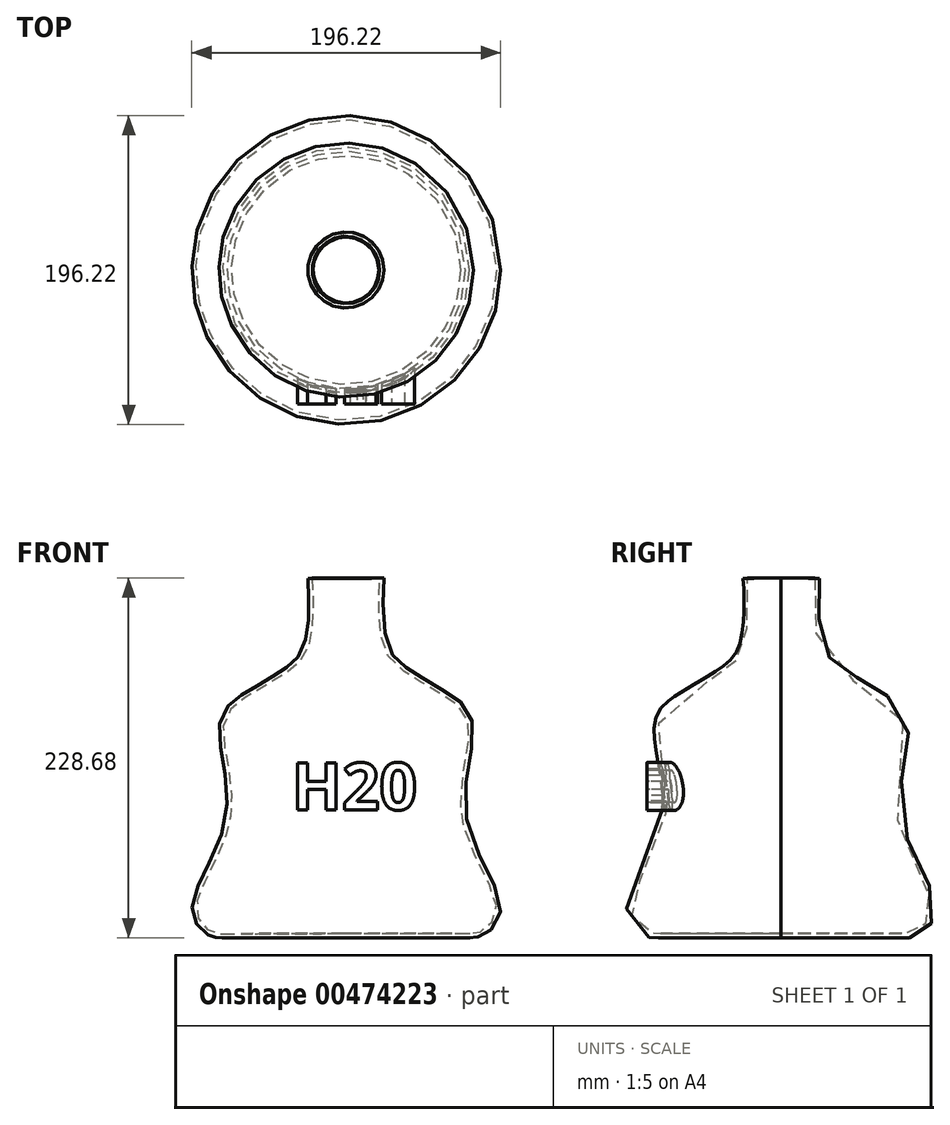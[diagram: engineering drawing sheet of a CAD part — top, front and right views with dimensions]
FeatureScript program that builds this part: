
annotation { "Feature Type Name" : "Feature", "Feature Type Description" : "" }
export const myFeature = defineFeature(function(context is Context, id is Id, definition is map)
    precondition{}
    {
        {
            var Q0;
            Q0=qCreatedBy(makeId("Front.planeOp"),FACE);
            var sketch = newSketch(context, id + "F0", { "sketchPlane" : qUnion([Q0])});
            skFitSpline(sketch, "E0", {"points": [v(0, 0) * mm, v(34.67, 0) * mm, v(59.42, 0) * mm, v(74.62, 0) * mm, v(80.36, 0) * mm, v(86.7, 1.46) * mm, v(98.07, 17.5) * mm, v(76.17, 76.9) * mm, v(79.96, 137.93) * mm, v(60.63, 157.65) * mm, v(39.03, 170.91) * mm, v(26.14, 186.45) * mm, v(23.9, 228.33) * mm], "startDerivative": vector(335.3, 0.36) * mm, "endDerivative": vector(16.6, 266.23) * mm});
            skFitSpline(sketch, "E1.0", {"points": [v(0, 2.7) * mm, v(3.5, 2.7) * mm, v(10.93, 2.7) * mm, v(20.66, 2.7) * mm, v(28.3, 2.7) * mm, v(33.86, 2.7) * mm, v(39.12, 2.7) * mm, v(44.12, 2.7) * mm, v(48.88, 2.7) * mm, v(53.45, 2.7) * mm, v(57.13, 2.7) * mm, v(60, 2.7) * mm, v(62.85, 2.7) * mm, v(66.27, 2.7) * mm, v(69.44, 2.71) * mm, v(71.75, 2.7) * mm, v(73.36, 2.7) * mm, v(74.82, 2.7) * mm, v(76.13, 2.69) * mm, v(77.3, 2.68) * mm, v(78.39, 2.67) * mm, v(79.23, 2.68) * mm, v(79.9, 2.69) * mm, v(80.4, 2.7) * mm, v(80.88, 2.71) * mm, v(81.5, 2.75) * mm, v(82.24, 2.82) * mm, v(83.13, 2.98) * mm, v(84.1, 3.26) * mm, v(85, 3.63) * mm, v(85.81, 4.03) * mm, v(86.68, 4.52) * mm, v(87.85, 5.28) * mm, v(89.28, 6.4) * mm, v(90.69, 7.7) * mm, v(92, 9.19) * mm, v(93.18, 10.83) * mm, v(94.16, 12.6) * mm, v(94.88, 14.5) * mm, v(95.33, 16.53) * mm, v(95.44, 18.67) * mm, v(95.2, 21.08) * mm, v(94.64, 23.73) * mm, v(93.76, 26.58) * mm, v(92.6, 29.63) * mm, v(90.75, 33.9) * mm, v(87.96, 39.63) * mm, v(84.22, 47) * mm, v(80.47, 54.78) * mm, v(77.62, 61.57) * mm, v(75.7, 67.16) * mm, v(74.5, 71.43) * mm, v(73.73, 75.04) * mm, v(73.28, 77.96) * mm, v(72.93, 80.88) * mm, v(72.7, 84.52) * mm, v(72.68, 90.32) * mm, v(73.21, 97.46) * mm, v(74.39, 105.77) * mm, v(75.78, 113.68) * mm, v(77.05, 121.08) * mm, v(77.76, 126.7) * mm, v(77.97, 130.76) * mm, v(77.92, 133.58) * mm, v(77.68, 135.7) * mm, v(77.36, 137.27) * mm, v(76.96, 138.75) * mm, v(76.29, 140.48) * mm, v(75.24, 142.4) * mm, v(73.97, 144.21) * mm, v(71.98, 146.48) * mm, v(69.01, 149.1) * mm, v(65.57, 151.48) * mm, v(62.65, 153.3) * mm, v(60.42, 154.64) * mm, v(58.16, 155.97) * mm, v(55.94, 157.29) * mm, v(53.75, 158.59) * mm, v(50.86, 160.3) * mm, v(47.35, 162.42) * mm, v(43.97, 164.5) * mm, v(41.36, 166.15) * mm, v(39.45, 167.39) * mm, v(37.91, 168.4) * mm, v(36.7, 169.23) * mm, v(34.9, 170.47) * mm, v(32.26, 172.43) * mm, v(28.99, 175.55) * mm, v(26.6, 178.77) * mm, v(25, 181.82) * mm, v(23.95, 184.36) * mm, v(23.08, 187.18) * mm, v(22.38, 190.22) * mm, v(21.82, 193.45) * mm, v(21.26, 197.95) * mm, v(20.82, 203.83) * mm, v(20.65, 210.95) * mm, v(20.74, 219.99) * mm, v(21.04, 225.7) * mm, v(21.21, 228.5) * mm]});
            skLineSegment(sketch, "E2", {"start": v(21.21, 228.5) * mm, "end": v(23.9, 228.33) * mm});
            skLineSegment(sketch, "E3", {"start": v(0, 2.7) * mm, "end": v(0, 0) * mm});
            skSolve(sketch);
        }
        {
            var Q0;
            Q0=makeQuery(id+"F0.imprint","IMPRINT",FACE,{"disambiguationData":[TD([[makeQuery(id+"F0.imprint","IMPRINT",EDGE,{"derivedFrom":sQuery(id+"F0.wireOp",EDGE,"E0")}),1.0]])]});
            var Q1;
            Q1=sQuery(id+"F0.wireOp",EDGE,"E3");
            revolve(context, id + "F1", {"entities" : qUnion([Q0]), "axis" : qUnion([Q1]), "revolveType" : RevolveType.FULL});
        }
        {
            var Q0;
            Q0=qCreatedBy(makeId("Front.planeOp"),FACE);
            cPlane(context, id + "F2", {"entities" : qUnion([Q0]), "cplaneType" : CPlaneType.OFFSET, "offset" : 85.1 * mm, "width" : 152.4 * mm, "height" : 152.4 * mm});
        }
        {
            var Q0;
            Q0=qCreatedBy(id+"F2.planeOp",FACE);
            var sketch = newSketch(context, id + "F3", { "sketchPlane" : qUnion([Q0])});
            skText(sketch, "E4", { "text": "H20", "fontName": "OpenSans-Bold.ttf"});
            const initialGuessF3  = {"E4": [-0.03472, 0.08118, 1, 0, 0.03004]};
            skSetInitialGuess(sketch, initialGuessF3);
            skSolve(sketch);
        }
        {
            var Q0;
            Q0 = qSketchRegion(id + "F3", true);
            var Q1;
            Q1 = qConstructionFilter(qBodyType(qCreatedBy(id + "F3" ,EDGE), BodyType.WIRE), ConstructionObject.NO);
            extrude(context, id + "F4", {"entities" : qUnion([Q0]), "surfaceEntities" : qUnion([Q1]), "endBound" : BoundingType.UP_TO_NEXT, "oppositeDirection" : true, "depth" : 25.4 * mm});
        }
    });
